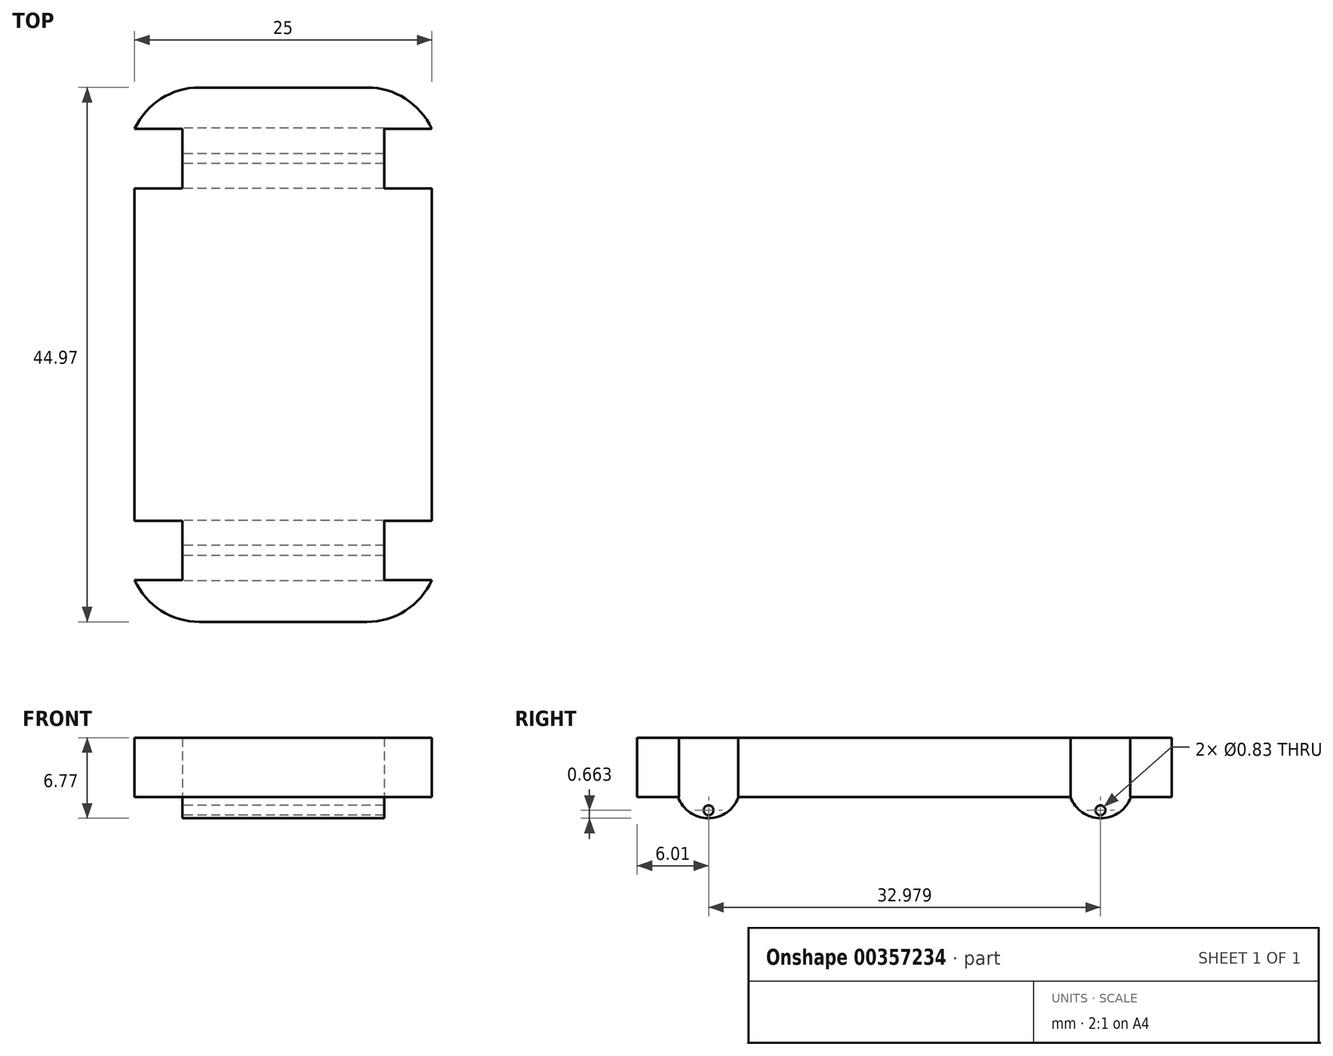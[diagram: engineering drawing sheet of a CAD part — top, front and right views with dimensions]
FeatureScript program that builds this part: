
annotation { "Feature Type Name" : "Feature", "Feature Type Description" : "" }
export const myFeature = defineFeature(function(context is Context, id is Id, definition is map)
    precondition{}
    {
        {
            var Q0;
            Q0=qCreatedBy(makeId("Top.planeOp"),FACE);
            var sketch = newSketch(context, id + "F0", { "sketchPlane" : qUnion([Q0])});
            skLineSegment(sketch, "E0.bottom", {"start": v(12.5, -22.5) * mm, "end": v(-12.5, -22.5) * mm});
            skLineSegment(sketch, "E0.top", {"start": v(10.5, 22.47) * mm, "end": v(-10.5, 22.47) * mm});
            skLineSegment(sketch, "E0.left", {"start": v(12.5, -22.5) * mm, "end": v(12.5, -19) * mm});
            skLineSegment(sketch, "E0.right", {"start": v(-12.5, -22.5) * mm, "end": v(-12.5, -19) * mm});
            skPoint(sketch, "E0.middle", {"position": v(0, 0) * mm});
            skLineSegment(sketch, "E1.bottom", {"start": v(-12.5, 19) * mm, "end": v(-8.5, 19) * mm});
            skLineSegment(sketch, "E1.top", {"start": v(-12.5, 14) * mm, "end": v(-8.5, 14) * mm});
            skLineSegment(sketch, "E1.right", {"start": v(-8.5, 19) * mm, "end": v(-8.5, 14) * mm});
            skLineSegment(sketch, "E2.MirrorCS", {"start": v(12.5, 19) * mm, "end": v(8.5, 19) * mm});
            skLineSegment(sketch, "E3.MirrorCS", {"start": v(8.5, 19) * mm, "end": v(8.5, 14) * mm});
            skLineSegment(sketch, "E4.MirrorCS", {"start": v(12.5, 14) * mm, "end": v(8.5, 14) * mm});
            skLineSegment(sketch, "E5.MirrorCS", {"start": v(-12.5, -14) * mm, "end": v(-8.5, -14) * mm});
            skLineSegment(sketch, "E6.MirrorCS", {"start": v(-8.5, -19) * mm, "end": v(-8.5, -14) * mm});
            skLineSegment(sketch, "E7.MirrorCS", {"start": v(-12.5, -19) * mm, "end": v(-8.5, -19) * mm});
            skLineSegment(sketch, "E8.MirrorCS", {"start": v(12.5, -14) * mm, "end": v(8.5, -14) * mm});
            skLineSegment(sketch, "E9.MirrorCS", {"start": v(8.5, -19) * mm, "end": v(8.5, -14) * mm});
            skLineSegment(sketch, "E10.MirrorCS", {"start": v(12.5, -19) * mm, "end": v(8.5, -19) * mm});
            skLineSegment(sketch, "E11.trimOffspring", {"start": v(-12.5, -14) * mm, "end": v(-12.5, 14) * mm});
            skLineSegment(sketch, "E12.trimOffspring", {"start": v(12.5, -14) * mm, "end": v(12.5, 14) * mm});
            skLineSegment(sketch, "E13.trimOffspring", {"start": v(12.5, 19) * mm, "end": v(12.5, 20.5) * mm});
            skLineSegment(sketch, "E14.trimOffspring", {"start": v(-12.5, 19) * mm, "end": v(-12.5, 20.5) * mm});
            skLineSegment(sketch, "E15", {"start": v(-12.5, 20.5) * mm, "end": v(-12.5, 22.5) * mm});
            skLineSegment(sketch, "E16", {"start": v(-12.5, 22.5) * mm, "end": v(-10.5, 22.47) * mm});
            skLineSegment(sketch, "E17", {"start": v(10.5, 22.47) * mm, "end": v(12.5, 22.47) * mm});
            skLineSegment(sketch, "E18", {"start": v(12.5, 22.47) * mm, "end": v(12.5, 20.5) * mm});
            skSolve(sketch);
        }
        {
            var Q0;
            Q0 = qSketchRegion(id + "F0", true);
            extrude(context, id + "F1", {"entities" : qUnion([Q0]), "depth" : 5 * mm});
        }
        {
            var Q0;
            Q0=qCreatedBy(makeId("Right.planeOp"),FACE);
            var sketch = newSketch(context, id + "F2", { "sketchPlane" : qUnion([Q0])});
            skCircle(sketch, "E19", {"center": v(-16.49, -1.1) * mm, "radius": 0.41 * mm});
            skCircle(sketch, "E20.MirrorC", {"center": v(16.49, -1.1) * mm, "radius": 0.41 * mm});
            skArc(sketch, "E21", {"start": v(-19.05, 0) * mm, "mid": v(-16.51, -1.77) * mm, "end": v(-13.97, 0) * mm});
            skArc(sketch, "E22.MirrorCS", {"start": v(19.05, 0) * mm, "mid": v(16.51, -1.77) * mm, "end": v(13.97, 0) * mm});
            skLineSegment(sketch, "E23", {"start": v(-19.05, 0) * mm, "end": v(-13.97, 0) * mm});
            skLineSegment(sketch, "E24", {"start": v(13.97, 0) * mm, "end": v(19.05, 0) * mm});
            skSolve(sketch);
        }
        {
            var Q0;
            Q0 = qSketchRegion(id + "F2", true);
            extrude(context, id + "F3", {"entities" : qUnion([Q0]), "operationType" : NewBodyOperationType.ADD, "endBound" : BoundingType.SYMMETRIC, "depth" : 17 * mm});
        }
        {
            var Q0;
            Q0=makeQuery(id+"F1.opExtrude","SWEPT_EDGE",EDGE,{"disambiguationData":[OSD([sQuery(id+"F0.wireOp",EDGE,"E0.bottom"),sQuery(id+"F0.wireOp",EDGE,"E0.left")])]});
            var Q1;
            Q1=makeQuery(id+"F1.opExtrude","SWEPT_EDGE",EDGE,{"disambiguationData":[OSD([sQuery(id+"F0.wireOp",EDGE,"E0.bottom"),sQuery(id+"F0.wireOp",EDGE,"E0.right")])]});
            fillet(context, id + "F4", {"entities" : qUnion([Q0, Q1]), "radius" : 6 * mm, "tangentPropagation" : true, "allowEdgeOverflow" : false});
        }
        {
            var Q0;
            Q0=makeQuery(id+"F1.opExtrude","SWEPT_EDGE",EDGE,{"disambiguationData":[OSD([sQuery(id+"F0.wireOp",EDGE,"E15"),sQuery(id+"F0.wireOp",EDGE,"E16")])]});
            var Q1;
            Q1=makeQuery(id+"F1.opExtrude","SWEPT_EDGE",EDGE,{"disambiguationData":[OSD([sQuery(id+"F0.wireOp",EDGE,"E17"),sQuery(id+"F0.wireOp",EDGE,"E18")])]});
            fillet(context, id + "F5", {"entities" : qUnion([Q0, Q1]), "radius" : 6 * mm, "tangentPropagation" : true, "allowEdgeOverflow" : false});
        }
    });
